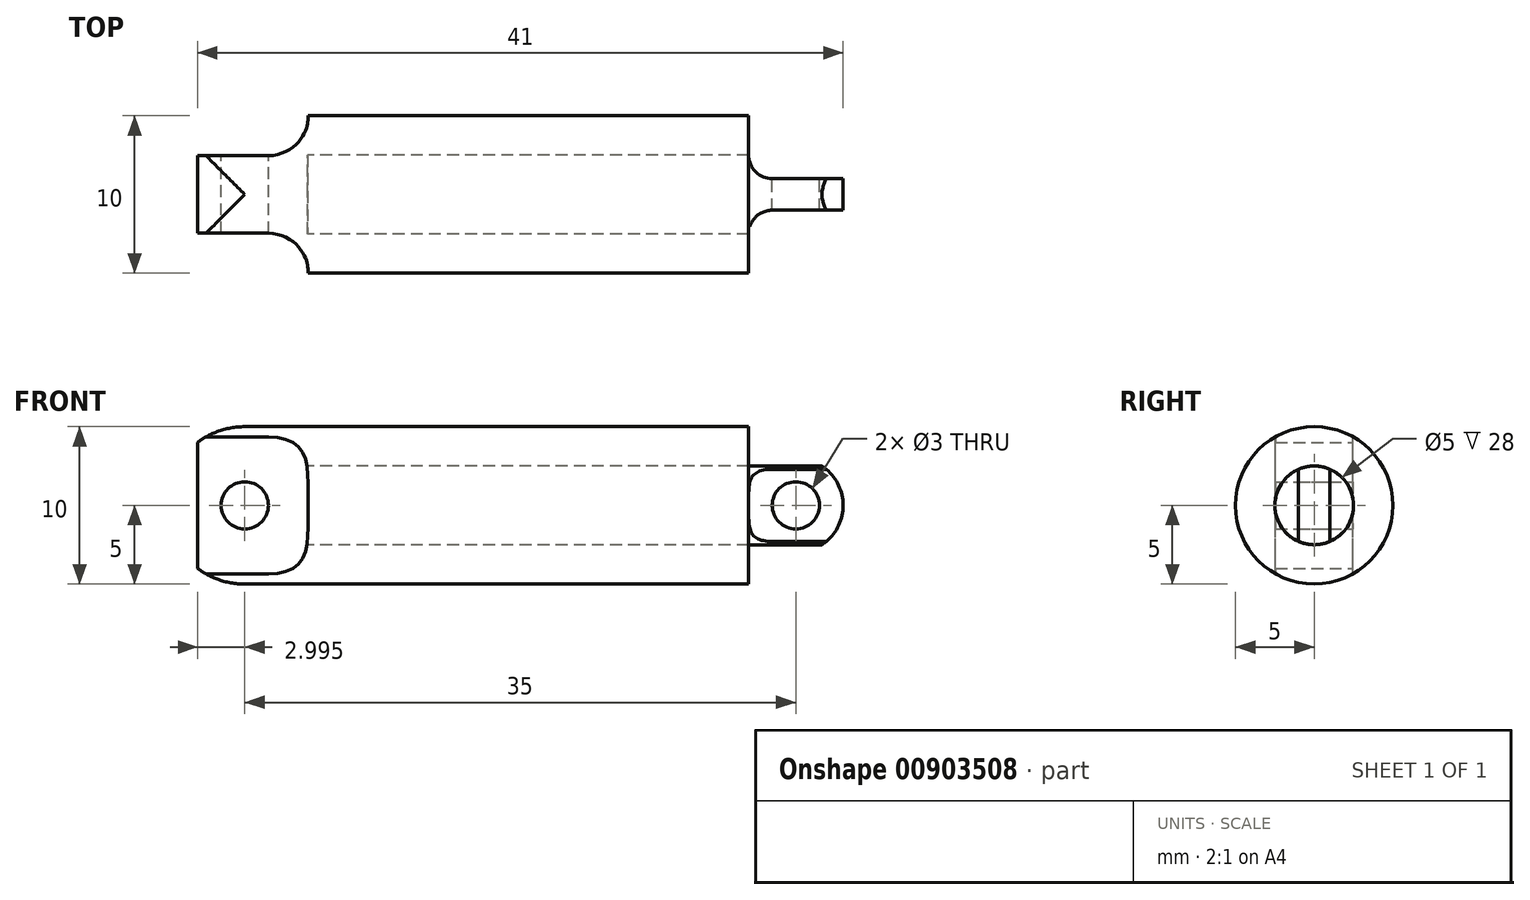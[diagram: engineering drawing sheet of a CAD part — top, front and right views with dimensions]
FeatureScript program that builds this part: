
annotation { "Feature Type Name" : "Feature", "Feature Type Description" : "" }
export const myFeature = defineFeature(function(context is Context, id is Id, definition is map)
    precondition{}
    {
        {
            var Q0;
            Q0=qCreatedBy(makeId("Top.planeOp"),FACE);
            var sketch = newSketch(context, id + "F0", { "sketchPlane" : qUnion([Q0])});
            skLineSegment(sketch, "E0", {"start": v(-33.33, 0) * mm, "end": v(32.61, 0) * mm, "construction": true});
            skLineSegment(sketch, "E1.bottom", {"start": v(-7.57, 2.5) * mm, "end": v(26.43, 2.5) * mm});
            skLineSegment(sketch, "E1.top", {"start": v(-7.57, 0) * mm, "end": v(26.43, 0) * mm});
            skLineSegment(sketch, "E1.right", {"start": v(26.43, 2.5) * mm, "end": v(26.43, 0) * mm});
            skLineSegment(sketch, "E2", {"start": v(23.43, 3.98) * mm, "end": v(23.43, -4.6) * mm, "construction": true});
            skLineSegment(sketch, "E3", {"start": v(20.43, 2.5) * mm, "end": v(20.43, 5) * mm});
            skLineSegment(sketch, "E4", {"start": v(20.43, 5) * mm, "end": v(-14.57, 5) * mm});
            skLineSegment(sketch, "E5", {"start": v(-14.57, 5) * mm, "end": v(-14.57, 0) * mm});
            skLineSegment(sketch, "E6", {"start": v(-11.57, 8.87) * mm, "end": v(-11.57, -6.02) * mm, "construction": true});
            skLineSegment(sketch, "E7", {"start": v(-7.57, 2.5) * mm, "end": v(-7.57, 0) * mm});
            skLineSegment(sketch, "E8", {"start": v(-14.57, 0) * mm, "end": v(-7.57, 0) * mm});
            skSolve(sketch);
        }
        {
            var Q0;
            Q0=makeQuery(id+"F0.imprint","IMPRINT",FACE,{"disambiguationData":[TD([[makeQuery(id+"F0.imprint","IMPRINT",EDGE,{"derivedFrom":sQuery(id+"F0.wireOp",EDGE,"E1.top")}),1.0]])]});
            var Q1;
            Q1=sQuery(id+"F0.wireOp",EDGE,"E0");
            revolve(context, id + "F1", {"surfaceOperationType" : NewSurfaceOperationType.NEW, "entities" : qUnion([Q0]), "axis" : qUnion([Q1]), "revolveType" : RevolveType.FULL});
        }
        {
            var Q0;
            {var subQ0=sQuery(id+"F0.wireOp",EDGE,"E3");Q0=makeQuery(id+"F0.imprint","IMPRINT",FACE,{"disambiguationData":[TD([[makeQuery(id+"F0.imprint","IMPRINT",EDGE,{"derivedFrom":subQ0}),1.0]])]});}
            var Q1;
            Q1=sQuery(id+"F0.wireOp",EDGE,"E0");
            revolve(context, id + "F2", {"surfaceOperationType" : NewSurfaceOperationType.NEW, "entities" : qUnion([Q0]), "axis" : qUnion([Q1]), "revolveType" : RevolveType.FULL});
        }
        {
            var Q0;
            Q0=qCreatedBy(makeId("Top.planeOp"),FACE);
            var sketch = newSketch(context, id + "F3", { "sketchPlane" : qUnion([Q0])});
            skLineSegment(sketch, "E9", {"start": v(26.43, 1) * mm, "end": v(21.93, 1) * mm});
            skArc(sketch, "E10", {"start": v(21.93, 1) * mm, "mid": v(20.86, 1.44) * mm, "end": v(20.43, 2.5) * mm});
            skLineSegment(sketch, "E11.0", {"start": v(-7.57, 2.5) * mm, "end": v(26.43, 2.5) * mm});
            skLineSegment(sketch, "E12", {"start": v(20.43, 2.5) * mm, "end": v(26.43, 2.5) * mm});
            skLineSegment(sketch, "E13", {"start": v(26.43, 1) * mm, "end": v(26.43, 2.5) * mm});
            skLineSegment(sketch, "E14.MirrorCS", {"start": v(26.43, -1) * mm, "end": v(26.43, -2.5) * mm});
            skLineSegment(sketch, "E15.MirrorCS", {"start": v(-7.57, -2.5) * mm, "end": v(26.43, -2.5) * mm});
            skArc(sketch, "E16.MirrorCS", {"start": v(21.93, -1) * mm, "mid": v(20.86, -1.44) * mm, "end": v(20.43, -2.5) * mm});
            skLineSegment(sketch, "E17.MirrorCS", {"start": v(26.43, -1) * mm, "end": v(21.93, -1) * mm});
            skLineSegment(sketch, "E18.0", {"start": v(-14.57, 5) * mm, "end": v(-14.57, 0) * mm});
            skLineSegment(sketch, "E19", {"start": v(-14.57, 5) * mm, "end": v(20.43, 5) * mm});
            skLineSegment(sketch, "E20", {"start": v(-14.57, 2.46) * mm, "end": v(-10.07, 2.46) * mm});
            skArc(sketch, "E21", {"start": v(-10.07, 2.46) * mm, "mid": v(-8.28, 3.2) * mm, "end": v(-7.54, 5) * mm});
            skLineSegment(sketch, "E22.MirrorCS", {"start": v(-14.57, -2.46) * mm, "end": v(-10.07, -2.46) * mm});
            skArc(sketch, "E23.MirrorCS", {"start": v(-10.07, -2.46) * mm, "mid": v(-8.28, -3.2) * mm, "end": v(-7.54, -5) * mm});
            skLineSegment(sketch, "E24.MirrorCS", {"start": v(-14.57, -5) * mm, "end": v(20.43, -5) * mm});
            skLineSegment(sketch, "E25.MirrorCS", {"start": v(-14.57, -5) * mm, "end": v(-14.57, 0) * mm});
            skSolve(sketch);
        }
        {
            var Q0;
            {var subQ0=sQuery(id+"F3.wireOp",EDGE,"E22.MirrorCS");Q0=makeQuery(id+"F3.imprint","IMPRINT",FACE,{"disambiguationData":[TD([[makeQuery(id+"F3.imprint","IMPRINT",EDGE,{"derivedFrom":subQ0}),-1.0]])]});}
            var Q1;
            {var subQ3=sQuery(id+"F3.wireOp",EDGE,"E20");Q1=makeQuery(id+"F3.imprint","IMPRINT",FACE,{"disambiguationData":[TD([[makeQuery(id+"F3.imprint","IMPRINT",EDGE,{"derivedFrom":subQ3}),1.0]])]});}
            var Q2;
            {var subQ0=sQuery(id+"F3.wireOp",EDGE,"E14.MirrorCS");Q2=makeQuery(id+"F3.imprint","IMPRINT",FACE,{"disambiguationData":[TD([[makeQuery(id+"F3.imprint","IMPRINT",EDGE,{"derivedFrom":subQ0}),-1.0]])]});}
            var Q3;
            Q3=makeQuery(id+"F3.imprint","IMPRINT",FACE,{"disambiguationData":[TD([[makeQuery(id+"F3.imprint","IMPRINT",EDGE,{"derivedFrom":sQuery(id+"F3.wireOp",EDGE,"E9")}),-1.0]])]});
            extrude(context, id + "F4", {"entities" : qUnion([Q0, Q1, Q2, Q3]), "operationType" : NewBodyOperationType.REMOVE, "endBound" : BoundingType.THROUGH_ALL, "oppositeDirection" : true, "depth" : 25 * mm, "offsetDistance" : 25 * mm, "hasSecondDirection" : true, "secondDirectionBound" : BoundingType.THROUGH_ALL, "secondDirectionOppositeDirection" : false, "secondDirectionDepth" : 25 * mm});
        }
        {
            var Q0;
            Q0=makeQuery(id+"F4.boolean.opBoolean","COPY",FACE,{"derivedFrom":makeQuery(id+"F4.opExtrude","SWEPT_FACE",FACE,{"disambiguationData":[OSD([sQuery(id+"F3.wireOp",EDGE,"E9")])]})});
            var sketch = newSketch(context, id + "F5", { "sketchPlane" : qUnion([Q0])});
            skCircle(sketch, "E26", {"center": v(-23.43, 0) * mm, "radius": 1.5 * mm});
            skCircle(sketch, "E27", {"center": v(-23.43, 0) * mm, "radius": 3 * mm});
            skLineSegment(sketch, "E28", {"start": v(-26.43, 2.5) * mm, "end": v(-25.08, 2.5) * mm});
            skLineSegment(sketch, "E29", {"start": v(-26.43, 0) * mm, "end": v(-26.43, 2.5) * mm});
            skLineSegment(sketch, "E30", {"start": v(-25.08, 2.5) * mm, "end": v(7.57, 2.5) * mm});
            skLineSegment(sketch, "E31.MirrorCS", {"start": v(-26.43, 0) * mm, "end": v(-26.43, -2.5) * mm});
            skLineSegment(sketch, "E32.MirrorCS", {"start": v(-26.43, -2.5) * mm, "end": v(-25.08, -2.5) * mm});
            skSolve(sketch);
        }
        {
            var Q0;
            {var subQ0=sQuery(id+"F5.wireOp",EDGE,"E29");var subQ1=sQuery(id+"F5.wireOp",EDGE,"E27");var subQ2=makeQuery(id+"F5.imprint","INTERSECT",VERTEX,{"derivedFrom":[subQ1,subQ0,sQuery(id+"F5.wireOp",EDGE,"E31.MirrorCS")]});Q0=makeQuery(id+"F5.imprint","IMPRINT",FACE,{"disambiguationData":[TD([[makeQuery(id+"F5.imprint","IMPRINT",EDGE,{"disambiguationData":[TD([[subQ2,1.0]])],"derivedFrom":subQ1}),-1.0]])]});}
            var Q1;
            {var subQ0=sQuery(id+"F5.wireOp",EDGE,"E28");Q1=makeQuery(id+"F5.imprint","IMPRINT",FACE,{"disambiguationData":[TD([[makeQuery(id+"F5.imprint","IMPRINT",EDGE,{"derivedFrom":subQ0}),-1.0]])]});}
            var Q2;
            {var subQ0=sQuery(id+"F5.wireOp",EDGE,"E31.MirrorCS");var subQ1=sQuery(id+"F5.wireOp",EDGE,"E27");var subQ2=makeQuery(id+"F5.imprint","INTERSECT",VERTEX,{"derivedFrom":[subQ1,sQuery(id+"F5.wireOp",EDGE,"E29"),subQ0]});Q2=makeQuery(id+"F5.imprint","IMPRINT",FACE,{"disambiguationData":[TD([[makeQuery(id+"F5.imprint","IMPRINT",EDGE,{"disambiguationData":[TD([[subQ2,-1.0]])],"derivedFrom":subQ1}),-1.0]])]});}
            var Q3;
            {var subQ0=sQuery(id+"F5.wireOp",EDGE,"E32.MirrorCS");Q3=makeQuery(id+"F5.imprint","IMPRINT",FACE,{"disambiguationData":[TD([[makeQuery(id+"F5.imprint","IMPRINT",EDGE,{"derivedFrom":subQ0}),1.0]])]});}
            var Q4;
            Q4=makeQuery(id+"F5.imprint","IMPRINT",FACE,{"disambiguationData":[TD([[makeQuery(id+"F5.imprint","IMPRINT",EDGE,{"derivedFrom":sQuery(id+"F5.wireOp",EDGE,"E26")}),1.0]])]});
            extrude(context, id + "F6", {"entities" : qUnion([Q0, Q1, Q2, Q3, Q4]), "operationType" : NewBodyOperationType.REMOVE, "endBound" : BoundingType.THROUGH_ALL, "oppositeDirection" : true, "depth" : 25 * mm, "offsetDistance" : 25 * mm});
        }
        {
            var Q0;
            Q0=makeQuery(id+"F4.boolean.opBoolean","COPY",FACE,{"derivedFrom":makeQuery(id+"F4.opExtrude","SWEPT_FACE",FACE,{"disambiguationData":[OSD([sQuery(id+"F3.wireOp",EDGE,"E20")])]})});
            var sketch = newSketch(context, id + "F7", { "sketchPlane" : qUnion([Q0])});
            skCircle(sketch, "E33", {"center": v(11.57, 0) * mm, "radius": 1.5 * mm});
            skLineSegment(sketch, "E34", {"start": v(-20.43, 5) * mm, "end": v(14.57, 5) * mm});
            skLineSegment(sketch, "E35.0", {"start": v(14.57, 4.35) * mm, "end": v(14.57, 5) * mm});
            skCircle(sketch, "E36", {"center": v(11.57, 0) * mm, "radius": 5 * mm});
            skLineSegment(sketch, "E37", {"start": v(14.57, -5) * mm, "end": v(-20.43, -5) * mm});
            skLineSegment(sketch, "E38.0", {"start": v(14.57, -4.35) * mm, "end": v(14.57, -5) * mm});
            skSolve(sketch);
        }
        {
            var Q0;
            {var subQ0=sQuery(id+"F7.wireOp",EDGE,"E36");var subQ1=sQuery(id+"F3.wireOp",EDGE,"E20");var subQ2=makeQuery(id+"F4.boolean.opBoolean","COPY",EDGE,{"derivedFrom":makeQuery(id+"F4.opExtrude","SWEPT_EDGE",EDGE,{"disambiguationData":[OSD([sQuery(id+"F3.wireOp",EDGE,"E18.0"),subQ1])]})});var subQ3=makeQuery(id+"F7.imprint","INTERSECT",VERTEX,{"disambiguationData":[OD(1.0)],"derivedFrom":[subQ2,subQ0]});Q0=makeQuery(id+"F7.imprint","IMPRINT",FACE,{"disambiguationData":[TD([[makeQuery(id+"F7.imprint","IMPRINT",EDGE,{"disambiguationData":[TD([[subQ3,1.0]])],"derivedFrom":subQ0}),-1.0]])]});}
            var Q1;
            {var subQ6=sQuery(id+"F7.wireOp",EDGE,"E38.0");Q1=makeQuery(id+"F7.imprint","IMPRINT",FACE,{"disambiguationData":[TD([[makeQuery(id+"F7.imprint","IMPRINT",EDGE,{"derivedFrom":subQ6}),-1.0]])]});}
            var Q2;
            {var subQ0=sQuery(id+"F7.wireOp",EDGE,"E36");var subQ1=sQuery(id+"F3.wireOp",EDGE,"E20");var subQ2=makeQuery(id+"F4.boolean.opBoolean","COPY",EDGE,{"derivedFrom":makeQuery(id+"F4.opExtrude","SWEPT_EDGE",EDGE,{"disambiguationData":[OSD([sQuery(id+"F3.wireOp",EDGE,"E18.0"),subQ1])]})});var subQ3=makeQuery(id+"F7.imprint","INTERSECT",VERTEX,{"disambiguationData":[OD(0.0)],"derivedFrom":[subQ2,subQ0]});Q2=makeQuery(id+"F7.imprint","IMPRINT",FACE,{"disambiguationData":[TD([[makeQuery(id+"F7.imprint","IMPRINT",EDGE,{"disambiguationData":[TD([[subQ3,-1.0]])],"derivedFrom":subQ0}),-1.0]])]});}
            var Q3;
            {var subQ0=sQuery(id+"F7.wireOp",EDGE,"E35.0");Q3=makeQuery(id+"F7.imprint","IMPRINT",FACE,{"disambiguationData":[TD([[makeQuery(id+"F7.imprint","IMPRINT",EDGE,{"derivedFrom":subQ0}),1.0]])]});}
            var Q4;
            Q4=makeQuery(id+"F7.imprint","IMPRINT",FACE,{"disambiguationData":[TD([[makeQuery(id+"F7.imprint","IMPRINT",EDGE,{"derivedFrom":sQuery(id+"F7.wireOp",EDGE,"E33")}),1.0]])]});
            extrude(context, id + "F8", {"entities" : qUnion([Q0, Q1, Q2, Q3, Q4]), "operationType" : NewBodyOperationType.REMOVE, "endBound" : BoundingType.THROUGH_ALL, "oppositeDirection" : true, "depth" : 25 * mm, "offsetDistance" : 25 * mm});
        }
    });
